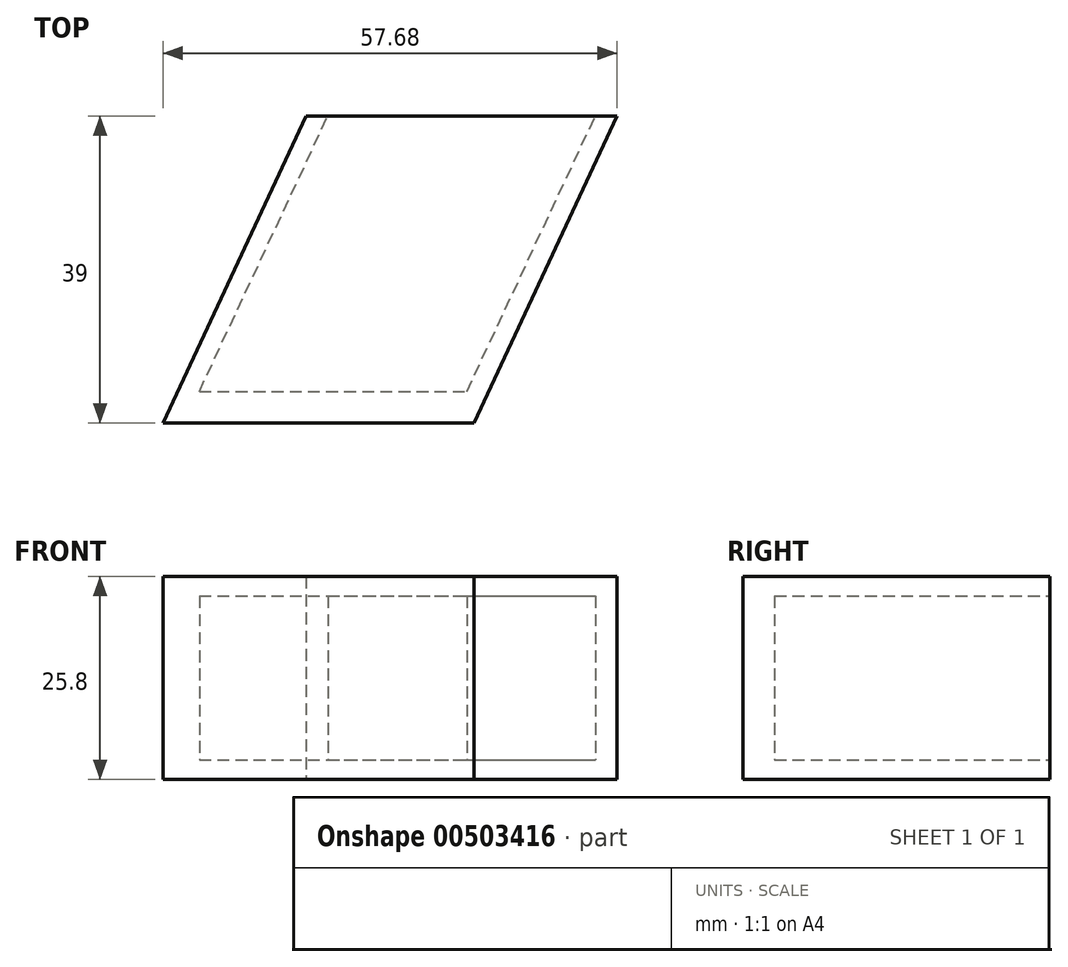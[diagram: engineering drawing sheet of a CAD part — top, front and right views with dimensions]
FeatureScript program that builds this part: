
annotation { "Feature Type Name" : "Feature", "Feature Type Description" : "" }
export const myFeature = defineFeature(function(context is Context, id is Id, definition is map)
    precondition{}
    {
        {
            var Q0;
            Q0=qCreatedBy(makeId("Top.planeOp"),FACE);
            var sketch = newSketch(context, id + "F0", { "sketchPlane" : qUnion([Q0])});
            skLineSegment(sketch, "E0", {"start": v(0, 0) * mm, "end": v(33.98, 0) * mm});
            skLineSegment(sketch, "E1", {"start": v(0, 0) * mm, "end": v(16.32, 35) * mm});
            skLineSegment(sketch, "E2.0", {"start": v(-4.62, -4) * mm, "end": v(13.56, 35) * mm});
            skLineSegment(sketch, "E3.0", {"start": v(34.88, -4) * mm, "end": v(53.06, 35) * mm});
            skLineSegment(sketch, "E4.0", {"start": v(-4.62, -4) * mm, "end": v(34.88, -4) * mm});
            skLineSegment(sketch, "E5.0", {"start": v(13.56, 35) * mm, "end": v(16.32, 35) * mm});
            skLineSegment(sketch, "E6.trimOffspring", {"start": v(50.3, 35) * mm, "end": v(53.06, 35) * mm});
            skLineSegment(sketch, "E7.trimOffspring", {"start": v(33.98, 0) * mm, "end": v(50.3, 35) * mm});
            skSolve(sketch);
        }
        {
            var Q0;
            Q0=makeQuery(id+"F0.imprint","IMPRINT",FACE,{"disambiguationData":[TD([[makeQuery(id+"F0.imprint","IMPRINT",EDGE,{"derivedFrom":sQuery(id+"F0.wireOp",EDGE,"E0")}),-1.0]])]});
            extrude(context, id + "F1", {"entities" : qUnion([Q0]), "depth" : 20.8 * mm});
        }
        {
            var Q0;
            Q0=makeQuery(id+"F1.opExtrude","CAP_FACE",FACE,{"disambiguationData":[OSD([sQuery(id+"F0.wireOp",EDGE,"E0"),sQuery(id+"F0.wireOp",EDGE,"E1"),sQuery(id+"F0.wireOp",EDGE,"E2.0"),sQuery(id+"F0.wireOp",EDGE,"E3.0"),sQuery(id+"F0.wireOp",EDGE,"E4.0"),sQuery(id+"F0.wireOp",EDGE,"E5.0"),sQuery(id+"F0.wireOp",EDGE,"E6.trimOffspring"),sQuery(id+"F0.wireOp",EDGE,"E7.trimOffspring")])],"isStart":false});
            var sketch = newSketch(context, id + "F2", { "sketchPlane" : qUnion([Q0])});
            skLineSegment(sketch, "E8", {"start": v(13.56, 35) * mm, "end": v(53.06, 35) * mm});
            skLineSegment(sketch, "E9", {"start": v(53.06, 35) * mm, "end": v(34.88, -4) * mm});
            skLineSegment(sketch, "E10", {"start": v(34.88, -4) * mm, "end": v(-4.62, -4) * mm});
            skLineSegment(sketch, "E11", {"start": v(-4.62, -4) * mm, "end": v(13.56, 35) * mm});
            skSolve(sketch);
        }
        {
            var Q0;
            Q0=makeQuery(id+"F2.imprint","IMPRINT",FACE,{"disambiguationData":[TD([[makeQuery(id+"F2.imprint","IMPRINT",EDGE,{"derivedFrom":makeQuery(id+"F1.opExtrude","CAP_EDGE",EDGE,{"disambiguationData":[OSD([sQuery(id+"F0.wireOp",EDGE,"E0")])],"isStart":false})}),1.0]])]});
            var Q1;
            {var subQ0=sQuery(id+"F2.wireOp",EDGE,"E9");Q1=makeQuery(id+"F2.imprint","IMPRINT",FACE,{"disambiguationData":[TD([[makeQuery(id+"F2.imprint","IMPRINT",EDGE,{"derivedFrom":subQ0}),1.0]])]});}
            extrude(context, id + "F3", {"entities" : qUnion([Q0, Q1]), "operationType" : NewBodyOperationType.ADD, "depth" : 2.5 * mm});
        }
        {
            var Q0;
            Q0=makeQuery(id+"F3.opExtrude","CAP_FACE",FACE,{"disambiguationData":[OSD([sQuery(id+"F2.wireOp",EDGE,"E8"),sQuery(id+"F2.wireOp",EDGE,"E9"),sQuery(id+"F2.wireOp",EDGE,"E10"),sQuery(id+"F2.wireOp",EDGE,"E11")])],"isStart":false});
            extrude(context, id + "F4", {"entities" : qUnion([Q0]), "operationType" : NewBodyOperationType.ADD, "oppositeDirection" : true, "depth" : 25.8 * mm, "hasSecondDirection" : true, "secondDirectionOppositeDirection" : true, "secondDirectionDepth" : (20.8 + 2.5) * mm});
        }
    });
